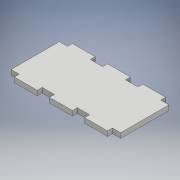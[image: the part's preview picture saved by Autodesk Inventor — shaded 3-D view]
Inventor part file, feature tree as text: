
AUTODESK INVENTOR PART (.ipt)
format: ipt  version: 2018 (Build 220112000, 112)  size: 192,512 bytes
history: native  units: mm
features: extrude x8, sketch x8, other x1
ambient origin geometry x8: Origin, YZ Plane, XZ Plane, XY Plane, X Axis, Y Axis, Z Axis, Center Point
bodies: Body1 (feature_tree)
feature tree (17):
  other  "Sólido1"
  extrude  "Extrusión1"  Depth=3.0mm
  extrude  "Extrusión2"  Depth=9.0mm
  extrude  "Extrusión3"  Depth=10.0mm TaperAngle=0.0deg
  extrude  "Extrusión4"  Depth=3.0mm TaperAngle=0.0deg
  extrude  "Extrusión5"  Depth=67.0mm
  extrude  "Extrusión6"  Depth=3.0mm TaperAngle=0.0deg
  extrude  "Extrusión7"  [1 undecoded]
  extrude  "Extrusión8"  [1 undecoded]
  sketch  "Boceto1"  dims[d19=3.0mm d20=0.0mm d23=7.0mm]
  sketch  "Boceto2"  dims[d24=10.0mm d25=0.0mm d26=9.0mm]
  sketch  "Boceto3"  dims[d27=10.0mm d28=0.0mm d29=10.0mm d30=0.0mm]
  sketch  "Boceto4"  dims[d32=3.0mm d33=0.0mm d34=3.0mm d35=0.0mm]
  sketch  "Boceto5"  dims[d36=5.0mm d37=67.0mm]
  sketch  "Boceto6"  dims[d38=29.5mm d39=0.0mm d40=3.0mm d41=0.0mm]
  sketch  "Boceto7"
  sketch  "Boceto8"
note: 2 required parameter values undecoded (feature->parameter linkage not recoverable at this tier; creation-order binding heuristic only, values carry confidence <= 0.55)
